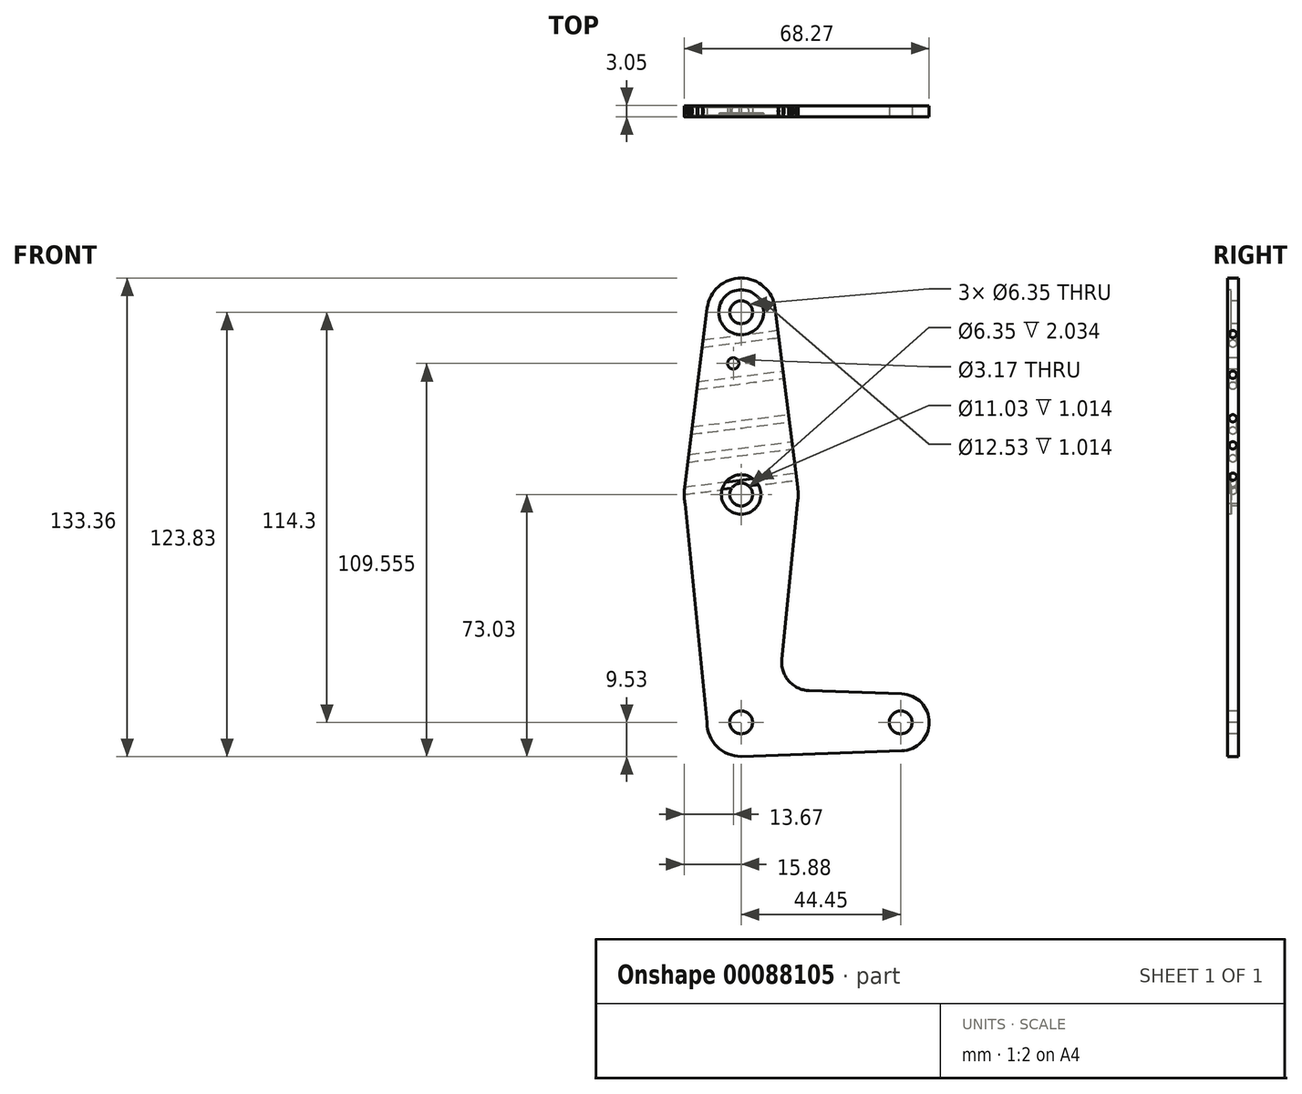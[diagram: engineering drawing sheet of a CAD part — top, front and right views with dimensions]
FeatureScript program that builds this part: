
annotation { "Feature Type Name" : "Feature", "Feature Type Description" : "" }
export const myFeature = defineFeature(function(context is Context, id is Id, definition is map)
    precondition{}
    {
        {
            var Q0;
            Q0=qCreatedBy(makeId("Front.planeOp"),FACE);
            var sketch = newSketch(context, id + "F0", { "sketchPlane" : qUnion([Q0])});
            skLineSegment(sketch, "E0", {"start": v(0, 0) * mm, "end": v(0, 114.3) * mm, "construction": true});
            skLineSegment(sketch, "E1", {"start": v(0, 0) * mm, "end": v(44.45, 0) * mm, "construction": true});
            skCircle(sketch, "E2", {"center": v(0, 114.3) * mm, "radius": 9.53 * mm});
            skCircle(sketch, "E3", {"center": v(0, 63.5) * mm, "radius": 15.88 * mm});
            skCircle(sketch, "E4", {"center": v(0, 0) * mm, "radius": 9.53 * mm});
            skCircle(sketch, "E5", {"center": v(44.45, 0) * mm, "radius": 7.94 * mm});
            skLineSegment(sketch, "E6", {"start": v(9.45, 115.5) * mm, "end": v(15.75, 65.48) * mm});
            skLineSegment(sketch, "E7", {"start": v(-9.45, 115.5) * mm, "end": v(-15.75, 65.48) * mm});
            skLineSegment(sketch, "E8", {"start": v(-15.74, 61.69) * mm, "end": v(-9.52, 0) * mm});
            skLineSegment(sketch, "E9", {"start": v(15.8, 61.9) * mm, "end": v(11.3, 17.6) * mm});
            skLineSegment(sketch, "E10", {"start": v(18.93, 8.85) * mm, "end": v(44.73, 7.93) * mm});
            skLineSegment(sketch, "E11", {"start": v(0, -9.53) * mm, "end": v(44.73, -7.93) * mm});
            skCircle(sketch, "E12", {"center": v(0, 114.3) * mm, "radius": 3.18 * mm});
            skCircle(sketch, "E13", {"center": v(0, 63.5) * mm, "radius": 3.18 * mm});
            skCircle(sketch, "E14", {"center": v(0, 0) * mm, "radius": 3.18 * mm});
            skCircle(sketch, "E15", {"center": v(44.45, 0) * mm, "radius": 3.18 * mm});
            skCircle(sketch, "E16", {"center": v(-2.2, 100.03) * mm, "radius": 1.59 * mm});
            skArc(sketch, "E17.filletArc", {"start": v(11.3, 17.6) * mm, "mid": v(13.22, 11.57) * mm, "end": v(18.93, 8.85) * mm});
            skSolve(sketch);
        }
        {
            var Q0;
            Q0=makeQuery(id+"F0.imprint","IMPRINT",FACE,{"disambiguationData":[TD([[makeQuery(id+"F0.imprint","IMPRINT",EDGE,{"derivedFrom":sQuery(id+"F0.wireOp",EDGE,"E12")}),-1.0]])]});
            var Q1;
            Q1=makeQuery(id+"F0.imprint","IMPRINT",FACE,{"disambiguationData":[TD([[makeQuery(id+"F0.imprint","IMPRINT",EDGE,{"derivedFrom":sQuery(id+"F0.wireOp",EDGE,"E15")}),-1.0]])]});
            var Q2;
            {var subQ1=sQuery(id+"F0.wireOp",EDGE,"E6");Q2=makeQuery(id+"F0.imprint","IMPRINT",FACE,{"disambiguationData":[TD([[makeQuery(id+"F0.imprint","IMPRINT",EDGE,{"derivedFrom":subQ1}),-1.0]])]});}
            var Q3;
            Q3=makeQuery(id+"F0.imprint","IMPRINT",FACE,{"disambiguationData":[TD([[makeQuery(id+"F0.imprint","IMPRINT",EDGE,{"derivedFrom":sQuery(id+"F0.wireOp",EDGE,"E13")}),-1.0]])]});
            var Q4;
            {var subQ10=sQuery(id+"F0.wireOp",EDGE,"E9");Q4=makeQuery(id+"F0.imprint","IMPRINT",FACE,{"disambiguationData":[TD([[makeQuery(id+"F0.imprint","IMPRINT",EDGE,{"derivedFrom":subQ10}),-1.0]])]});}
            var Q5;
            Q5=makeQuery(id+"F0.imprint","IMPRINT",FACE,{"disambiguationData":[TD([[makeQuery(id+"F0.imprint","IMPRINT",EDGE,{"derivedFrom":sQuery(id+"F0.wireOp",EDGE,"E14")}),-1.0]])]});
            var Q6;
            {var subQ0=sQuery(id+"F0.wireOp",EDGE,"E11");var subQ1=sQuery(id+"F0.wireOp",EDGE,"E4");var subQ2=makeQuery(id+"F0.imprint","INTERSECT",VERTEX,{"disambiguationData":[OD(0.0)],"derivedFrom":[subQ1,subQ0]});Q6=makeQuery(id+"F0.imprint","IMPRINT",FACE,{"disambiguationData":[TD([[makeQuery(id+"F0.imprint","IMPRINT",EDGE,{"disambiguationData":[TD([[subQ2,-1.0]])],"derivedFrom":subQ1}),1.0]])]});}
            extrude(context, id + "F1", {"entities" : qUnion([Q0, Q1, Q2, Q3, Q4, Q5, Q6]), "oppositeDirection" : true, "depth" : 3.05 * mm});
        }
        {
            var Q0;
            Q0=makeQuery(id+"F1.opExtrude","CAP_FACE",FACE,{"disambiguationData":[OSD([sQuery(id+"F0.wireOp",EDGE,"E2"),sQuery(id+"F0.wireOp",EDGE,"E3"),sQuery(id+"F0.wireOp",EDGE,"E4"),sQuery(id+"F0.wireOp",EDGE,"E5"),sQuery(id+"F0.wireOp",EDGE,"E6"),sQuery(id+"F0.wireOp",EDGE,"E7"),sQuery(id+"F0.wireOp",EDGE,"E8"),sQuery(id+"F0.wireOp",EDGE,"E9"),sQuery(id+"F0.wireOp",EDGE,"E10"),sQuery(id+"F0.wireOp",EDGE,"E11"),sQuery(id+"F0.wireOp",EDGE,"E12"),sQuery(id+"F0.wireOp",EDGE,"E13"),sQuery(id+"F0.wireOp",EDGE,"E14"),sQuery(id+"F0.wireOp",EDGE,"E15"),sQuery(id+"F0.wireOp",EDGE,"E16"),sQuery(id+"F0.wireOp",EDGE,"E17.filletArc")])],"isStart":true});
            var sketch = newSketch(context, id + "F2", { "sketchPlane" : qUnion([Q0])});
            skCircle(sketch, "E18", {"center": v(0, 63.5) * mm, "radius": 5.51 * mm});
            skCircle(sketch, "E19", {"center": v(44.45, 0) * mm, "radius": 5.27 * mm});
            skCircle(sketch, "E20", {"center": v(0, 114.3) * mm, "radius": 6.26 * mm});
            skSolve(sketch);
        }
        {
            var Q0;
            Q0=makeQuery(id+"F2.imprint","IMPRINT",FACE,{"disambiguationData":[TD([[makeQuery(id+"F2.imprint","IMPRINT",EDGE,{"derivedFrom":sQuery(id+"F2.wireOp",EDGE,"E20")}),1.0]])]});
            var Q1;
            Q1=makeQuery(id+"F2.imprint","IMPRINT",FACE,{"disambiguationData":[TD([[makeQuery(id+"F2.imprint","IMPRINT",EDGE,{"derivedFrom":sQuery(id+"F2.wireOp",EDGE,"E18")}),1.0]])]});
            extrude(context, id + "F3", {"entities" : qUnion([Q0, Q1]), "operationType" : NewBodyOperationType.REMOVE, "oppositeDirection" : true, "depth" : 1.01 * mm});
        }
        {
            var Q0;
            Q0=makeQuery(id+"F1.opExtrude","SWEPT_FACE",FACE,{"disambiguationData":[OSD([sQuery(id+"F0.wireOp",EDGE,"E6")])]});
            var sketch = newSketch(context, id + "F4", { "sketchPlane" : qUnion([Q0])});
            skCircle(sketch, "E21", {"center": v(1.52, 66.03) * mm, "radius": 1.03 * mm});
            skCircle(sketch, "E22", {"center": v(1.52, 74.83) * mm, "radius": 1.03 * mm});
            skCircle(sketch, "E23", {"center": v(1.52, 82.43) * mm, "radius": 1.03 * mm});
            skCircle(sketch, "E24", {"center": v(1.52, 94.65) * mm, "radius": 1.03 * mm});
            skCircle(sketch, "E25", {"center": v(1.52, 106.1) * mm, "radius": 1.03 * mm});
            skLineSegment(sketch, "E26", {"start": v(1.52, 63) * mm, "end": v(1.52, 126.3) * mm, "construction": true});
            skSolve(sketch);
        }
        {
            var Q0;
            Q0=makeQuery(id+"F4.imprint","IMPRINT",FACE,{"disambiguationData":[TD([[makeQuery(id+"F4.imprint","IMPRINT",EDGE,{"derivedFrom":sQuery(id+"F4.wireOp",EDGE,"E21")}),1.0]])]});
            var Q1;
            Q1=makeQuery(id+"F4.imprint","IMPRINT",FACE,{"disambiguationData":[TD([[makeQuery(id+"F4.imprint","IMPRINT",EDGE,{"derivedFrom":sQuery(id+"F4.wireOp",EDGE,"E22")}),1.0]])]});
            var Q2;
            Q2=makeQuery(id+"F4.imprint","IMPRINT",FACE,{"disambiguationData":[TD([[makeQuery(id+"F4.imprint","IMPRINT",EDGE,{"derivedFrom":sQuery(id+"F4.wireOp",EDGE,"E23")}),1.0]])]});
            var Q3;
            Q3=makeQuery(id+"F4.imprint","IMPRINT",FACE,{"disambiguationData":[TD([[makeQuery(id+"F4.imprint","IMPRINT",EDGE,{"derivedFrom":sQuery(id+"F4.wireOp",EDGE,"E24")}),1.0]])]});
            var Q4;
            Q4=makeQuery(id+"F4.imprint","IMPRINT",FACE,{"disambiguationData":[TD([[makeQuery(id+"F4.imprint","IMPRINT",EDGE,{"derivedFrom":sQuery(id+"F4.wireOp",EDGE,"E25")}),1.0]])]});
            extrude(context, id + "F5", {"entities" : qUnion([Q0, Q1, Q2, Q3, Q4]), "operationType" : NewBodyOperationType.REMOVE, "oppositeDirection" : true, "depth" : 34.5 * mm});
        }
    });
